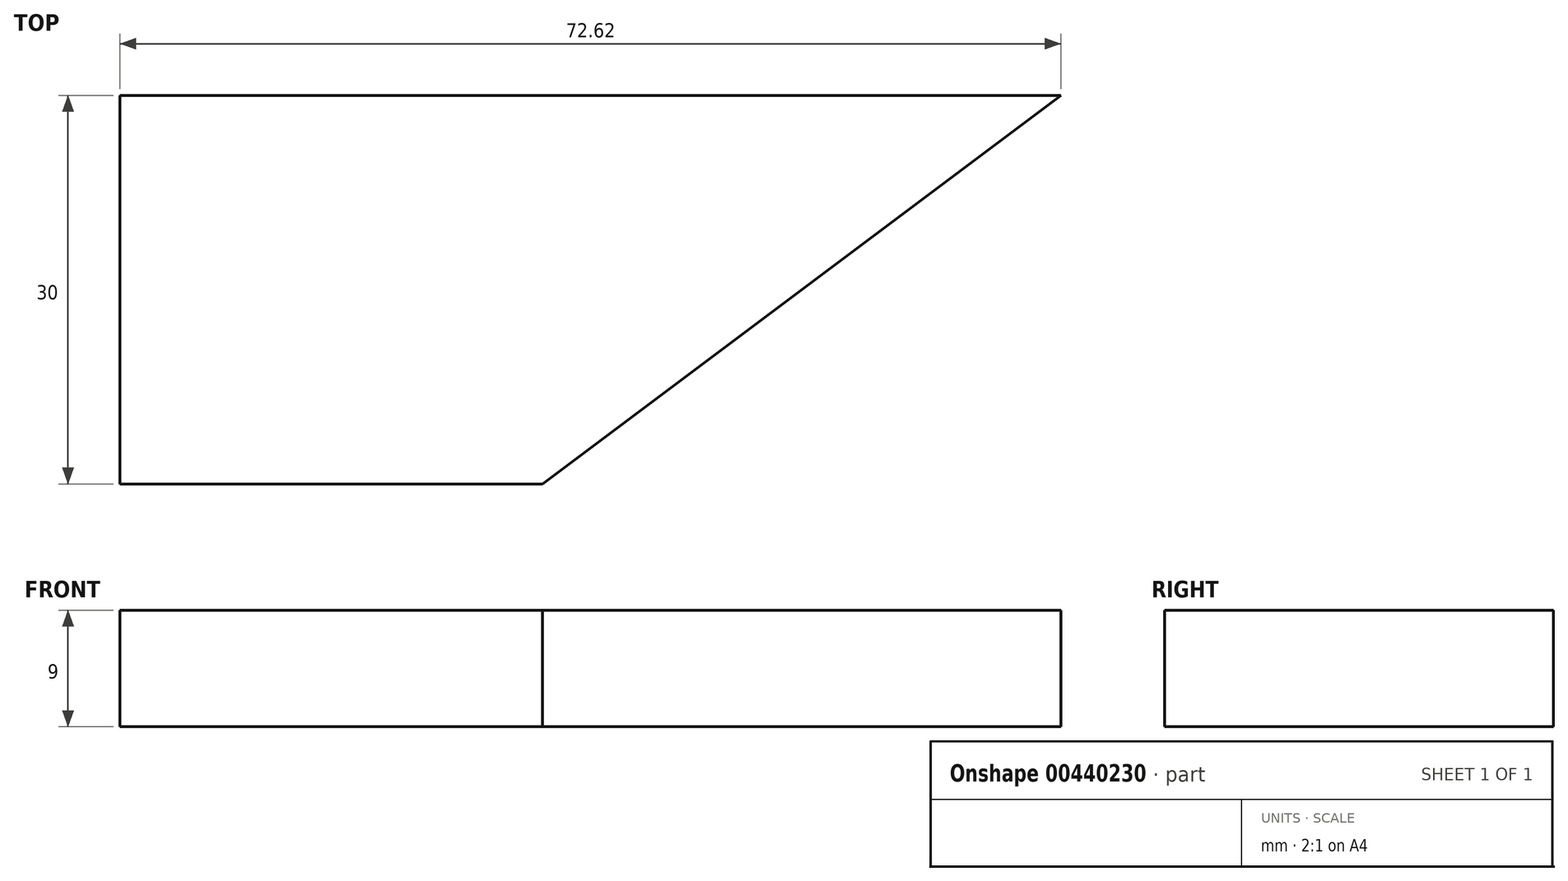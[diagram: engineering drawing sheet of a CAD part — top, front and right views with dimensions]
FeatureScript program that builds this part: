
annotation { "Feature Type Name" : "Feature", "Feature Type Description" : "" }
export const myFeature = defineFeature(function(context is Context, id is Id, definition is map)
    precondition{}
    {
        {
            var Q0;
            Q0=qCreatedBy(makeId("Top.planeOp"),FACE);
            var sketch = newSketch(context, id + "F0", { "sketchPlane" : qUnion([Q0])});
            skLineSegment(sketch, "E0.bottom", {"start": v(-16.3, 15) * mm, "end": v(16.3, 15) * mm});
            skLineSegment(sketch, "E0.top", {"start": v(-16.3, -15) * mm, "end": v(16.3, -15) * mm});
            skLineSegment(sketch, "E0.left", {"start": v(-16.3, 15) * mm, "end": v(-16.3, -15) * mm});
            skLineSegment(sketch, "E0.right", {"start": v(16.3, 15) * mm, "end": v(16.3, -15) * mm});
            skPoint(sketch, "E0.middle", {"position": v(0, 0) * mm});
            skLineSegment(sketch, "E1", {"start": v(16.3, 15) * mm, "end": v(56.3, 15) * mm});
            skLineSegment(sketch, "E2", {"start": v(16.3, -15) * mm, "end": v(56.3, 15) * mm});
            skSolve(sketch);
        }
        {
            var Q0;
            Q0=makeQuery(id+"F0.imprint","IMPRINT",FACE,{"disambiguationData":[TD([[makeQuery(id+"F0.imprint","IMPRINT",EDGE,{"derivedFrom":sQuery(id+"F0.wireOp",EDGE,"E0.bottom")}),-1.0]])]});
            var Q1;
            Q1=makeQuery(id+"F0.imprint","IMPRINT",FACE,{"disambiguationData":[TD([[makeQuery(id+"F0.imprint","IMPRINT",EDGE,{"derivedFrom":sQuery(id+"F0.wireOp",EDGE,"E0.right")}),1.0]])]});
            extrude(context, id + "F1", {"entities" : qUnion([Q0, Q1]), "depth" : 9 * mm});
        }
    });
